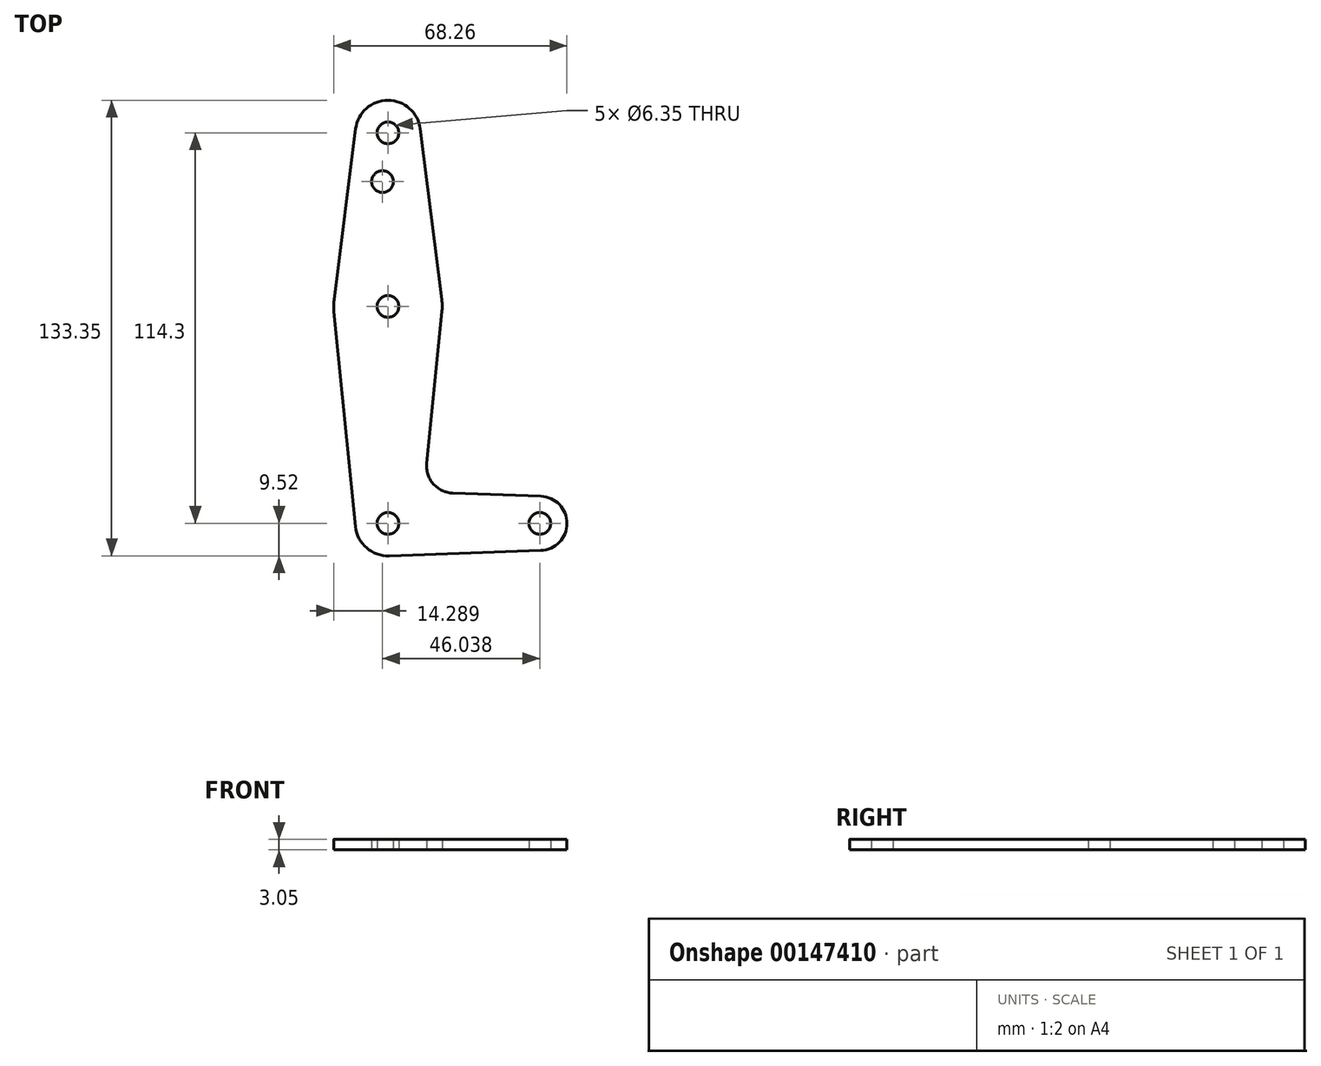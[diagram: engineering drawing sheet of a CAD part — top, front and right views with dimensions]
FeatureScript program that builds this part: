
annotation { "Feature Type Name" : "Feature", "Feature Type Description" : "" }
export const myFeature = defineFeature(function(context is Context, id is Id, definition is map)
    precondition{}
    {
        {
            var Q0;
            Q0=qCreatedBy(makeId("Top.planeOp"),FACE);
            var sketch = newSketch(context, id + "F0", { "sketchPlane" : qUnion([Q0])});
            skLineSegment(sketch, "E0", {"start": v(-44.73, 68.87) * mm, "end": v(-44.73, -45.43) * mm, "construction": true});
            skLineSegment(sketch, "E1", {"start": v(-44.73, -45.43) * mm, "end": v(-0.28, -45.43) * mm, "construction": true});
            skCircle(sketch, "E2", {"center": v(-44.73, 68.87) * mm, "radius": 9.53 * mm});
            skCircle(sketch, "E3", {"center": v(-44.73, -45.43) * mm, "radius": 9.53 * mm});
            skCircle(sketch, "E4", {"center": v(-0.28, -45.43) * mm, "radius": 7.94 * mm});
            skCircle(sketch, "E5", {"center": v(-44.73, 18.07) * mm, "radius": 15.88 * mm});
            skLineSegment(sketch, "E6", {"start": v(-54.18, 70.06) * mm, "end": v(-60.48, 20.05) * mm});
            skLineSegment(sketch, "E7", {"start": v(-35.28, 70.06) * mm, "end": v(-28.98, 20.05) * mm});
            skLineSegment(sketch, "E8", {"start": v(-28.94, 16.48) * mm, "end": v(-33.4, -27.84) * mm});
            skLineSegment(sketch, "E9", {"start": v(-60.53, 16.48) * mm, "end": v(-54.21, -46.38) * mm});
            skLineSegment(sketch, "E10", {"start": v(-44.4, -54.95) * mm, "end": v(0, -53.36) * mm});
            skLineSegment(sketch, "E11", {"start": v(-25.77, -36.58) * mm, "end": v(0, -37.5) * mm});
            skCircle(sketch, "E12", {"center": v(-0.28, -45.43) * mm, "radius": 3.18 * mm});
            skCircle(sketch, "E13", {"center": v(-44.73, -45.43) * mm, "radius": 3.18 * mm});
            skCircle(sketch, "E14", {"center": v(-46.32, 54.6) * mm, "radius": 3.18 * mm});
            skCircle(sketch, "E15", {"center": v(-44.73, 18.07) * mm, "radius": 3.18 * mm});
            skCircle(sketch, "E16", {"center": v(-44.73, 68.87) * mm, "radius": 3.18 * mm});
            skArc(sketch, "E17.filletArc", {"start": v(-33.4, -27.84) * mm, "mid": v(-31.47, -33.86) * mm, "end": v(-25.77, -36.58) * mm});
            skSolve(sketch);
        }
        {
            var Q0;
            Q0=makeQuery(id+"F0.imprint","IMPRINT",FACE,{"disambiguationData":[TD([[makeQuery(id+"F0.imprint","IMPRINT",EDGE,{"derivedFrom":sQuery(id+"F0.wireOp",EDGE,"E16")}),-1.0]])]});
            var Q1;
            {var subQ1=sQuery(id+"F0.wireOp",EDGE,"E6");Q1=makeQuery(id+"F0.imprint","IMPRINT",FACE,{"disambiguationData":[TD([[makeQuery(id+"F0.imprint","IMPRINT",EDGE,{"derivedFrom":subQ1}),1.0]])]});}
            var Q2;
            Q2=makeQuery(id+"F0.imprint","IMPRINT",FACE,{"disambiguationData":[TD([[makeQuery(id+"F0.imprint","IMPRINT",EDGE,{"derivedFrom":sQuery(id+"F0.wireOp",EDGE,"E15")}),-1.0]])]});
            var Q3;
            {var subQ0=sQuery(id+"F0.wireOp",EDGE,"E8");Q3=makeQuery(id+"F0.imprint","IMPRINT",FACE,{"disambiguationData":[TD([[makeQuery(id+"F0.imprint","IMPRINT",EDGE,{"derivedFrom":subQ0}),-1.0]])]});}
            var Q4;
            Q4=makeQuery(id+"F0.imprint","IMPRINT",FACE,{"disambiguationData":[TD([[makeQuery(id+"F0.imprint","IMPRINT",EDGE,{"derivedFrom":sQuery(id+"F0.wireOp",EDGE,"E13")}),-1.0]])]});
            var Q5;
            Q5=makeQuery(id+"F0.imprint","IMPRINT",FACE,{"disambiguationData":[TD([[makeQuery(id+"F0.imprint","IMPRINT",EDGE,{"derivedFrom":sQuery(id+"F0.wireOp",EDGE,"E12")}),-1.0]])]});
            extrude(context, id + "F1", {"entities" : qUnion([Q0, Q1, Q2, Q3, Q4, Q5]), "depth" : 3.05 * mm});
        }
    });
